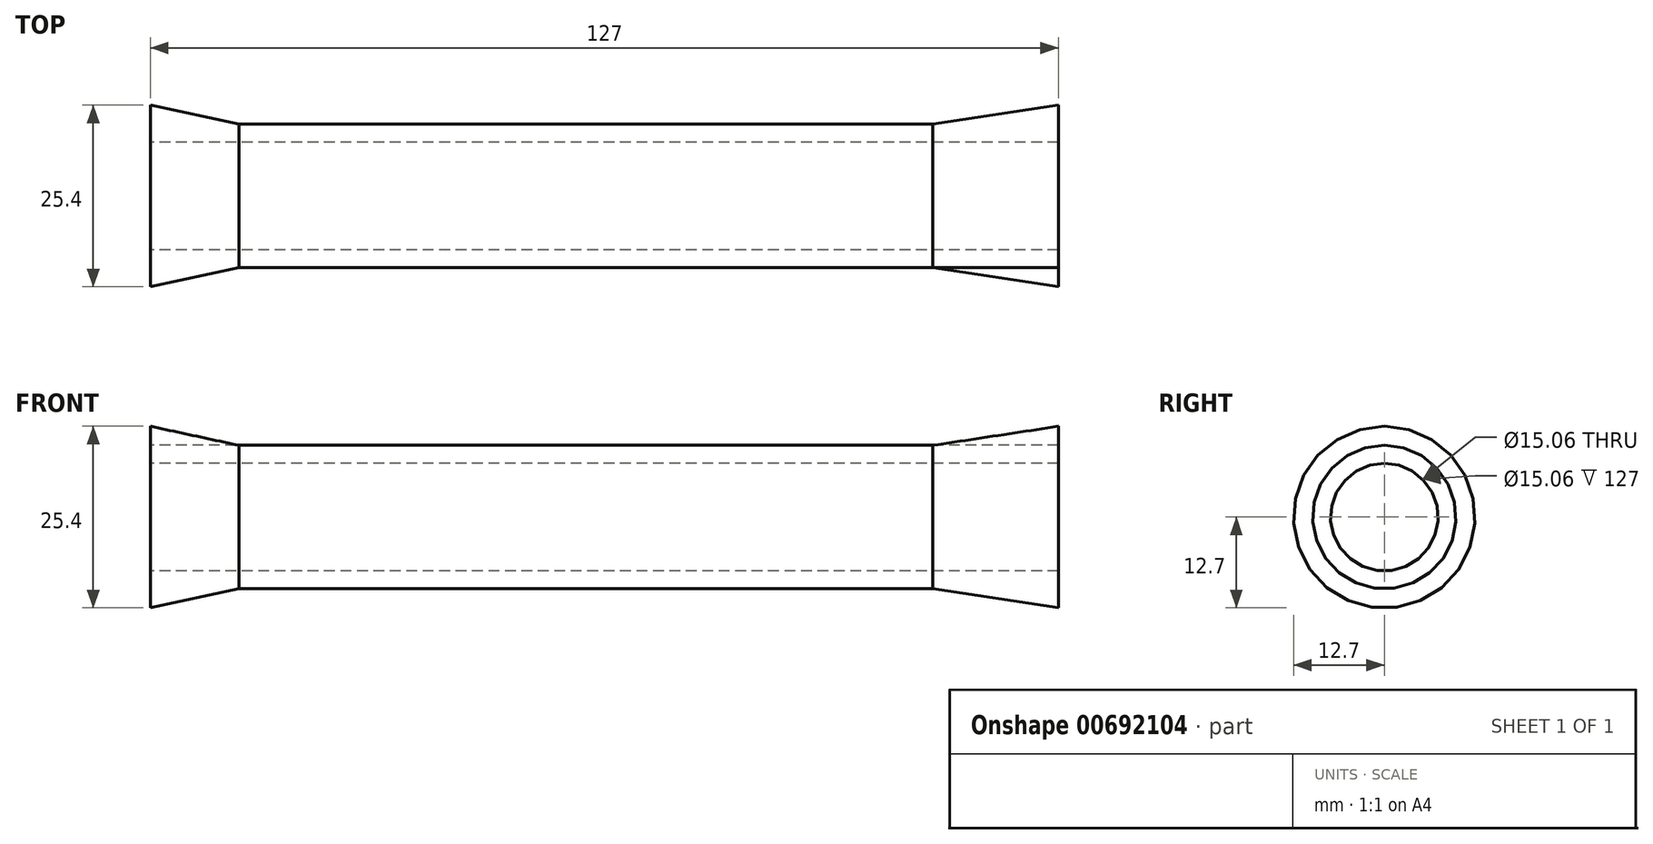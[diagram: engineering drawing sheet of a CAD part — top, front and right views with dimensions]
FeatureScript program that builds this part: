
annotation { "Feature Type Name" : "Feature", "Feature Type Description" : "" }
export const myFeature = defineFeature(function(context is Context, id is Id, definition is map)
    precondition{}
    {
        {
            var Q0;
            Q0=qCreatedBy(makeId("Front.planeOp"),FACE);
            var sketch = newSketch(context, id + "F0", { "sketchPlane" : qUnion([Q0])});
            skLineSegment(sketch, "E0.bottom", {"start": v(114.3, 10.03) * mm, "end": v(-114.3, 10.03) * mm});
            skLineSegment(sketch, "E0.top", {"start": v(114.3, -10.03) * mm, "end": v(-114.3, -10.03) * mm});
            skLineSegment(sketch, "E0.left", {"start": v(114.3, 10.03) * mm, "end": v(114.3, -10.03) * mm});
            skLineSegment(sketch, "E0.right", {"start": v(-114.3, 10.03) * mm, "end": v(-114.3, -10.03) * mm});
            skPoint(sketch, "E0.middle", {"position": v(0, 0) * mm});
            skLineSegment(sketch, "E1.bottom", {"start": v(-114.3, 12.7) * mm, "end": v(-63.5, 12.7) * mm});
            skLineSegment(sketch, "E1.top", {"start": v(-114.3, -12.7) * mm, "end": v(-63.5, -12.7) * mm});
            skLineSegment(sketch, "E1.left", {"start": v(-114.3, 12.7) * mm, "end": v(-114.3, -12.7) * mm});
            skLineSegment(sketch, "E1.right", {"start": v(-63.5, 12.7) * mm, "end": v(-63.5, -12.7) * mm});
            skPoint(sketch, "E1.middle", {"position": v(-86.28, 0) * mm});
            skLineSegment(sketch, "E2.MirrorCS", {"start": v(-114.3, -10.03) * mm, "end": v(-114.3, 10.03) * mm});
            skLineSegment(sketch, "E3.MirrorCS", {"start": v(-63.5, -12.7) * mm, "end": v(-63.5, 12.7) * mm});
            skLineSegment(sketch, "E4.MirrorCS", {"start": v(-114.3, -12.7) * mm, "end": v(-114.3, 12.7) * mm});
            skPoint(sketch, "E5.MirrorP", {"position": v(86.28, 0) * mm});
            skLineSegment(sketch, "E6.MirrorCS", {"start": v(114.3, 12.7) * mm, "end": v(114.3, -12.7) * mm});
            skLineSegment(sketch, "E7.MirrorCS", {"start": v(114.3, 12.7) * mm, "end": v(63.5, 12.7) * mm});
            skLineSegment(sketch, "E8.MirrorCS", {"start": v(63.5, 12.7) * mm, "end": v(63.5, -12.7) * mm});
            skLineSegment(sketch, "E9.MirrorCS", {"start": v(114.3, -10.03) * mm, "end": v(114.3, 10.03) * mm});
            skLineSegment(sketch, "E10.MirrorCS", {"start": v(114.3, -12.7) * mm, "end": v(63.5, -12.7) * mm});
            skLineSegment(sketch, "E11.MirrorCS", {"start": v(114.3, -12.7) * mm, "end": v(114.3, 12.7) * mm});
            skLineSegment(sketch, "E12.MirrorCS", {"start": v(63.5, -12.7) * mm, "end": v(63.5, 12.7) * mm});
            skLineSegment(sketch, "E13", {"start": v(-114.3, 0) * mm, "end": v(114.3, 0) * mm});
            skLineSegment(sketch, "E14", {"start": v(0, -10.03) * mm, "end": v(0, -7.53) * mm});
            skLineSegment(sketch, "E15.MirrorCS", {"start": v(0, 10.03) * mm, "end": v(0, 7.53) * mm});
            skLineSegment(sketch, "E16", {"start": v(0, 7.53) * mm, "end": v(114.3, 7.53) * mm});
            skLineSegment(sketch, "E17", {"start": v(114.3, 7.53) * mm, "end": v(-114.3, 7.53) * mm});
            skLineSegment(sketch, "E18", {"start": v(0, -7.53) * mm, "end": v(114.3, -7.53) * mm});
            skLineSegment(sketch, "E19", {"start": v(114.3, -7.53) * mm, "end": v(-114.3, -7.53) * mm});
            skLineSegment(sketch, "E20", {"start": v(-63.5, 12.7) * mm, "end": v(-51.08, 10.03) * mm});
            skLineSegment(sketch, "E21.MirrorCS", {"start": v(-63.5, -12.7) * mm, "end": v(-51.08, -10.03) * mm});
            skLineSegment(sketch, "E22", {"start": v(63.5, 12.7) * mm, "end": v(45.92, 10.03) * mm});
            skLineSegment(sketch, "E23.MirrorCS", {"start": v(63.5, -12.7) * mm, "end": v(45.92, -10.03) * mm});
            skSolve(sketch);
        }
        {
            var Q0;
            {var subQ5=sQuery(id+"F0.wireOp",EDGE,"E1.bottom");Q0=makeQuery(id+"F0.imprint","IMPRINT",FACE,{"disambiguationData":[TD([[makeQuery(id+"F0.imprint","IMPRINT",EDGE,{"derivedFrom":subQ5}),-1.0]])]});}
            var Q1;
            {var subQ0=sQuery(id+"F0.wireOp",EDGE,"E4.MirrorCS");var subQ1=sQuery(id+"F0.wireOp",EDGE,"E0.bottom");var subQ2=makeQuery(id+"F0.imprint","INTERSECT",VERTEX,{"derivedFrom":[subQ1,subQ0]});Q1=makeQuery(id+"F0.imprint","IMPRINT",FACE,{"disambiguationData":[TD([[makeQuery(id+"F0.imprint","IMPRINT",EDGE,{"disambiguationData":[TD([[subQ2,1.0]])],"derivedFrom":subQ1}),1.0]])]});}
            var Q2;
            {var subQ5=sQuery(id+"F0.wireOp",EDGE,"E1.top");Q2=makeQuery(id+"F0.imprint","IMPRINT",FACE,{"disambiguationData":[TD([[makeQuery(id+"F0.imprint","IMPRINT",EDGE,{"derivedFrom":subQ5}),1.0]])]});}
            var Q3;
            {var subQ0=sQuery(id+"F0.wireOp",EDGE,"E4.MirrorCS");var subQ1=sQuery(id+"F0.wireOp",EDGE,"E0.top");var subQ2=makeQuery(id+"F0.imprint","INTERSECT",VERTEX,{"derivedFrom":[subQ1,subQ0]});Q3=makeQuery(id+"F0.imprint","IMPRINT",FACE,{"disambiguationData":[TD([[makeQuery(id+"F0.imprint","IMPRINT",EDGE,{"disambiguationData":[TD([[subQ2,1.0]])],"derivedFrom":subQ1}),-1.0]])]});}
            var Q4;
            {var subQ0=sQuery(id+"F0.wireOp",EDGE,"E14");Q4=makeQuery(id+"F0.imprint","IMPRINT",FACE,{"disambiguationData":[TD([[makeQuery(id+"F0.imprint","IMPRINT",EDGE,{"derivedFrom":subQ0}),1.0]])]});}
            var Q5;
            {var subQ0=sQuery(id+"F0.wireOp",EDGE,"E15.MirrorCS");Q5=makeQuery(id+"F0.imprint","IMPRINT",FACE,{"disambiguationData":[TD([[makeQuery(id+"F0.imprint","IMPRINT",EDGE,{"derivedFrom":subQ0}),-1.0]])]});}
            var Q6;
            {var subQ0=sQuery(id+"F0.wireOp",EDGE,"E15.MirrorCS");Q6=makeQuery(id+"F0.imprint","IMPRINT",FACE,{"disambiguationData":[TD([[makeQuery(id+"F0.imprint","IMPRINT",EDGE,{"derivedFrom":subQ0}),1.0]])]});}
            var Q7;
            {var subQ0=sQuery(id+"F0.wireOp",EDGE,"E14");Q7=makeQuery(id+"F0.imprint","IMPRINT",FACE,{"disambiguationData":[TD([[makeQuery(id+"F0.imprint","IMPRINT",EDGE,{"derivedFrom":subQ0}),-1.0]])]});}
            var Q8;
            {var subQ0=sQuery(id+"F0.wireOp",EDGE,"E11.MirrorCS");var subQ1=sQuery(id+"F0.wireOp",EDGE,"E0.top");var subQ2=makeQuery(id+"F0.imprint","INTERSECT",VERTEX,{"derivedFrom":[subQ1,subQ0]});Q8=makeQuery(id+"F0.imprint","IMPRINT",FACE,{"disambiguationData":[TD([[makeQuery(id+"F0.imprint","IMPRINT",EDGE,{"disambiguationData":[TD([[subQ2,-1.0]])],"derivedFrom":subQ1}),-1.0]])]});}
            var Q9;
            {var subQ5=sQuery(id+"F0.wireOp",EDGE,"E10.MirrorCS");Q9=makeQuery(id+"F0.imprint","IMPRINT",FACE,{"disambiguationData":[TD([[makeQuery(id+"F0.imprint","IMPRINT",EDGE,{"derivedFrom":subQ5}),-1.0]])]});}
            var Q10;
            {var subQ5=sQuery(id+"F0.wireOp",EDGE,"E7.MirrorCS");Q10=makeQuery(id+"F0.imprint","IMPRINT",FACE,{"disambiguationData":[TD([[makeQuery(id+"F0.imprint","IMPRINT",EDGE,{"derivedFrom":subQ5}),1.0]])]});}
            var Q11;
            {var subQ0=sQuery(id+"F0.wireOp",EDGE,"E11.MirrorCS");var subQ1=sQuery(id+"F0.wireOp",EDGE,"E0.bottom");var subQ2=makeQuery(id+"F0.imprint","INTERSECT",VERTEX,{"derivedFrom":[subQ1,subQ0]});Q11=makeQuery(id+"F0.imprint","IMPRINT",FACE,{"disambiguationData":[TD([[makeQuery(id+"F0.imprint","IMPRINT",EDGE,{"disambiguationData":[TD([[subQ2,-1.0]])],"derivedFrom":subQ1}),1.0]])]});}
            var Q12;
            {var subQ0=sQuery(id+"F0.wireOp",EDGE,"E20");Q12=makeQuery(id+"F0.imprint","IMPRINT",FACE,{"disambiguationData":[TD([[makeQuery(id+"F0.imprint","IMPRINT",EDGE,{"derivedFrom":subQ0}),-1.0]])]});}
            var Q13;
            {var subQ0=sQuery(id+"F0.wireOp",EDGE,"E22");Q13=makeQuery(id+"F0.imprint","IMPRINT",FACE,{"disambiguationData":[TD([[makeQuery(id+"F0.imprint","IMPRINT",EDGE,{"derivedFrom":subQ0}),1.0]])]});}
            var Q14;
            Q14=sQuery(id+"F0.wireOp",EDGE,"E13");
            revolve(context, id + "F1", {"entities" : qUnion([Q0, Q1, Q2, Q3, Q4, Q5, Q6, Q7, Q8, Q9, Q10, Q11, Q12, Q13]), "axis" : qUnion([Q14]), "revolveType" : RevolveType.FULL});
        }
    });
